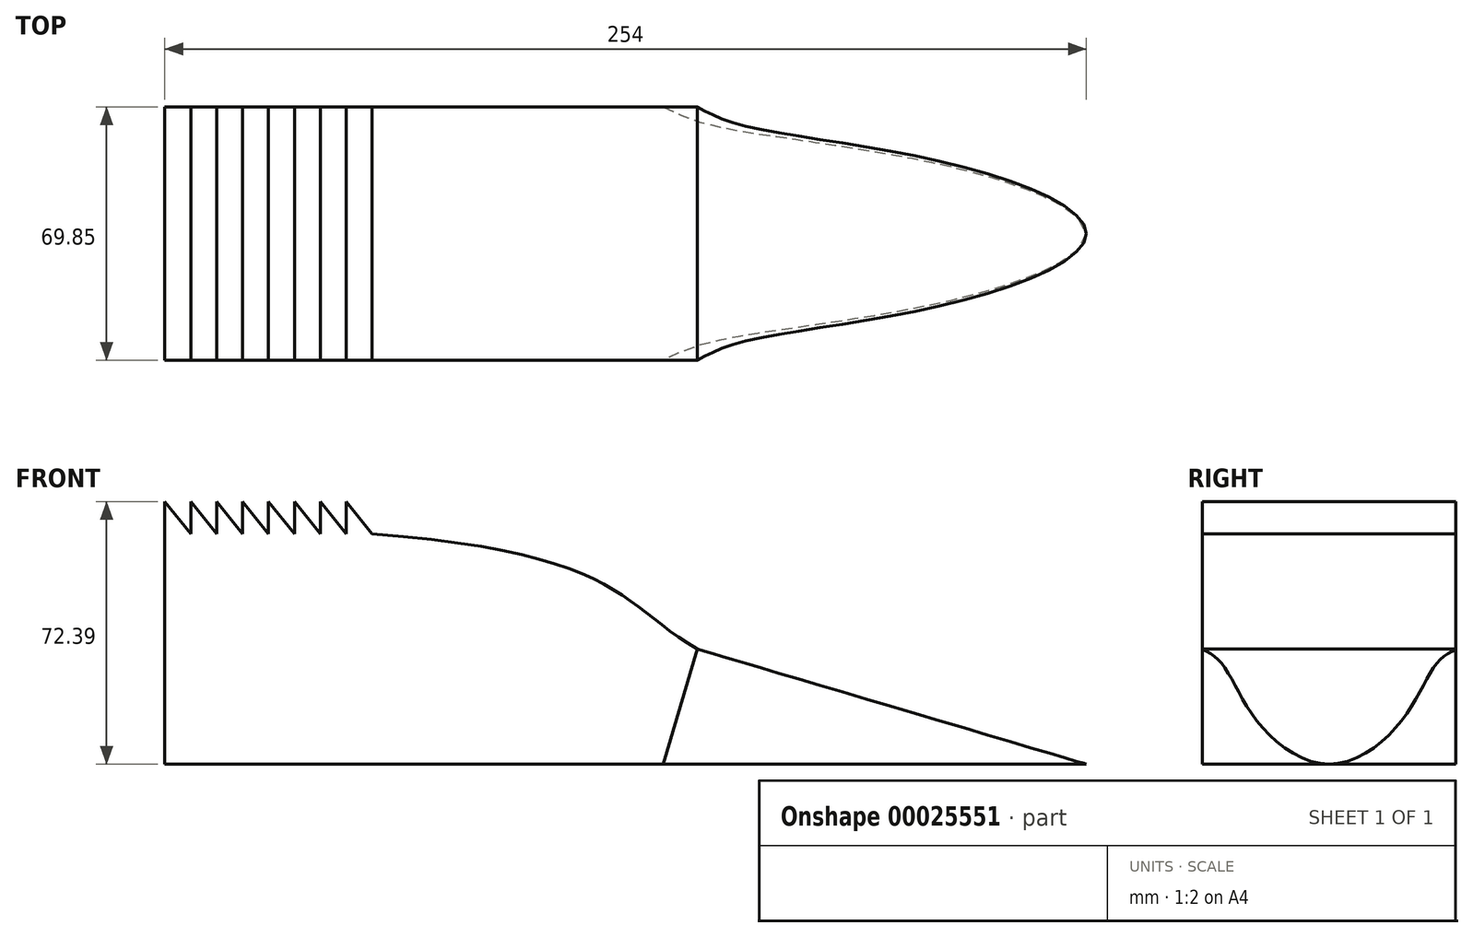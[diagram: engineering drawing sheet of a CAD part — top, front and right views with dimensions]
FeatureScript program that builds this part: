
annotation { "Feature Type Name" : "Feature", "Feature Type Description" : "" }
export const myFeature = defineFeature(function(context is Context, id is Id, definition is map)
    precondition{}
    {
        {
            var Q0;
            Q0=qCreatedBy(makeId("Front.planeOp"),FACE);
            var sketch = newSketch(context, id + "F0", { "sketchPlane" : qUnion([Q0])});
            skLineSegment(sketch, "E0.rect.bottom", {"start": v(-127, 31.75) * mm, "end": v(-69.85, 31.75) * mm});
            skLineSegment(sketch, "E0.rect.top", {"start": v(-127, -31.75) * mm, "end": v(127, -31.75) * mm});
            skLineSegment(sketch, "E0.rect.left", {"start": v(-127, 31.75) * mm, "end": v(-127, -31.75) * mm});
            skPoint(sketch, "E0.rect.middle", {"position": v(0, 0) * mm});
            skFitSpline(sketch, "E1", {"points": [v(-69.85, 31.75) * mm, v(19.83, 0) * mm, v(127, -31.75) * mm], "startDerivative": vector(429.65, -33.1) * mm, "endDerivative": vector(187.9, -30.92) * mm});
            skLineSegment(sketch, "E2", {"start": v(-127, 31.75) * mm, "end": v(-127, 40.64) * mm});
            skLineSegment(sketch, "E3", {"start": v(-127, 40.64) * mm, "end": v(-119.86, 31.75) * mm});
            skLineSegment(sketch, "E4", {"start": v(-119.86, 31.75) * mm, "end": v(-119.86, 40.64) * mm});
            skLineSegment(sketch, "E5", {"start": v(-119.86, 40.64) * mm, "end": v(-112.71, 31.75) * mm});
            skLineSegment(sketch, "E6", {"start": v(-112.71, 31.75) * mm, "end": v(-112.71, 40.64) * mm});
            skLineSegment(sketch, "E7", {"start": v(-112.71, 40.64) * mm, "end": v(-105.57, 31.75) * mm});
            skLineSegment(sketch, "E8", {"start": v(-105.57, 31.75) * mm, "end": v(-105.57, 40.64) * mm});
            skLineSegment(sketch, "E9", {"start": v(-105.57, 40.64) * mm, "end": v(-98.43, 31.75) * mm});
            skLineSegment(sketch, "E10", {"start": v(-98.43, 31.75) * mm, "end": v(-98.43, 40.64) * mm});
            skLineSegment(sketch, "E11", {"start": v(-98.43, 40.64) * mm, "end": v(-91.28, 31.75) * mm});
            skLineSegment(sketch, "E12", {"start": v(-91.28, 31.75) * mm, "end": v(-91.28, 40.64) * mm});
            skLineSegment(sketch, "E13", {"start": v(-91.28, 40.64) * mm, "end": v(-84.14, 31.75) * mm});
            skLineSegment(sketch, "E14", {"start": v(-84.14, 31.75) * mm, "end": v(-84.14, 40.64) * mm});
            skLineSegment(sketch, "E15", {"start": v(-84.14, 40.64) * mm, "end": v(-77, 31.75) * mm});
            skLineSegment(sketch, "E16", {"start": v(-77, 31.75) * mm, "end": v(-77, 40.64) * mm});
            skLineSegment(sketch, "E17", {"start": v(-77, 40.64) * mm, "end": v(-69.85, 31.75) * mm});
            skPoint(sketch, "E0.rect.right.start.orphan", {"position": v(127, 31.75) * mm});
            skLineSegment(sketch, "E18", {"start": v(19.83, 0) * mm, "end": v(127, -31.75) * mm});
            skSolve(sketch);
        }
        {
            var Q0;
            Q0 = qSketchRegion(id + "F0", true);
            extrude(context, id + "F1", {"entities" : qUnion([Q0]), "depth" : 69.85 * mm});
        }
        {
            var Q0;
            Q0=makeQuery(id+"F1.opExtrude","SWEPT_FACE",FACE,{"disambiguationData":[OSD([sQuery(id+"F0.wireOp",EDGE,"E18")])]});
            var sketch = newSketch(context, id + "F2", { "sketchPlane" : qUnion([Q0])});
            skPoint(sketch, "E19", {"position": v(31.71, -64.85) * mm});
            skPoint(sketch, "E20", {"position": v(31.71, -69.85) * mm});
            skPoint(sketch, "E21", {"position": v(31.71, -5) * mm});
            skPoint(sketch, "E22", {"position": v(31.71, 0) * mm});
            skPoint(sketch, "E23", {"position": v(130.79, -34.93) * mm});
            skPoint(sketch, "E24", {"position": v(95.21, -69.85) * mm});
            skPoint(sketch, "E25", {"position": v(95.21, 0) * mm});
            skLineSegment(sketch, "E26", {"start": v(95.21, -69.85) * mm, "end": v(95.21, -69.85) * mm});
            skLineSegment(sketch, "E27", {"start": v(95.21, 0) * mm, "end": v(95.21, 0) * mm});
            skPoint(sketch, "E28", {"position": v(95.21, -53.34) * mm});
            skPoint(sketch, "E29", {"position": v(95.21, -16.51) * mm});
            skFitSpline(sketch, "E30", {"points": [v(19.01, 0) * mm, v(31.71, -5) * mm, v(95.21, -16.51) * mm, v(130.79, -34.93) * mm, v(95.21, -53.34) * mm, v(31.71, -64.85) * mm, v(19.01, -69.85) * mm], "startDerivative": vector(96.73, -50.98) * mm, "endDerivative": vector(-96.73, -50.98) * mm});
            skSolve(sketch);
        }
        {
            var Q0;
            {var subQ0=sQuery(id+"F0.wireOp",EDGE,"E18");var subQ1=makeQuery(id+"F1.opExtrude","CAP_EDGE",EDGE,{"disambiguationData":[OSD([subQ0])],"isStart":false});Q0=makeQuery(id+"F2.imprint","IMPRINT",FACE,{"disambiguationData":[TD([[makeQuery(id+"F2.imprint","IMPRINT",EDGE,{"derivedFrom":subQ1}),1.0]])]});}
            var Q1;
            {var subQ1=sQuery(id+"F0.wireOp",EDGE,"E18");var subQ5=makeQuery(id+"F1.opExtrude","CAP_EDGE",EDGE,{"disambiguationData":[OSD([subQ1])],"isStart":true});Q1=makeQuery(id+"F2.imprint","IMPRINT",FACE,{"disambiguationData":[TD([[makeQuery(id+"F2.imprint","IMPRINT",EDGE,{"derivedFrom":subQ5}),-1.0]])]});}
            extrude(context, id + "F3", {"entities" : qUnion([Q0, Q1]), "operationType" : NewBodyOperationType.REMOVE, "oppositeDirection" : true, "depth" : 76.2 * mm});
        }
    });
